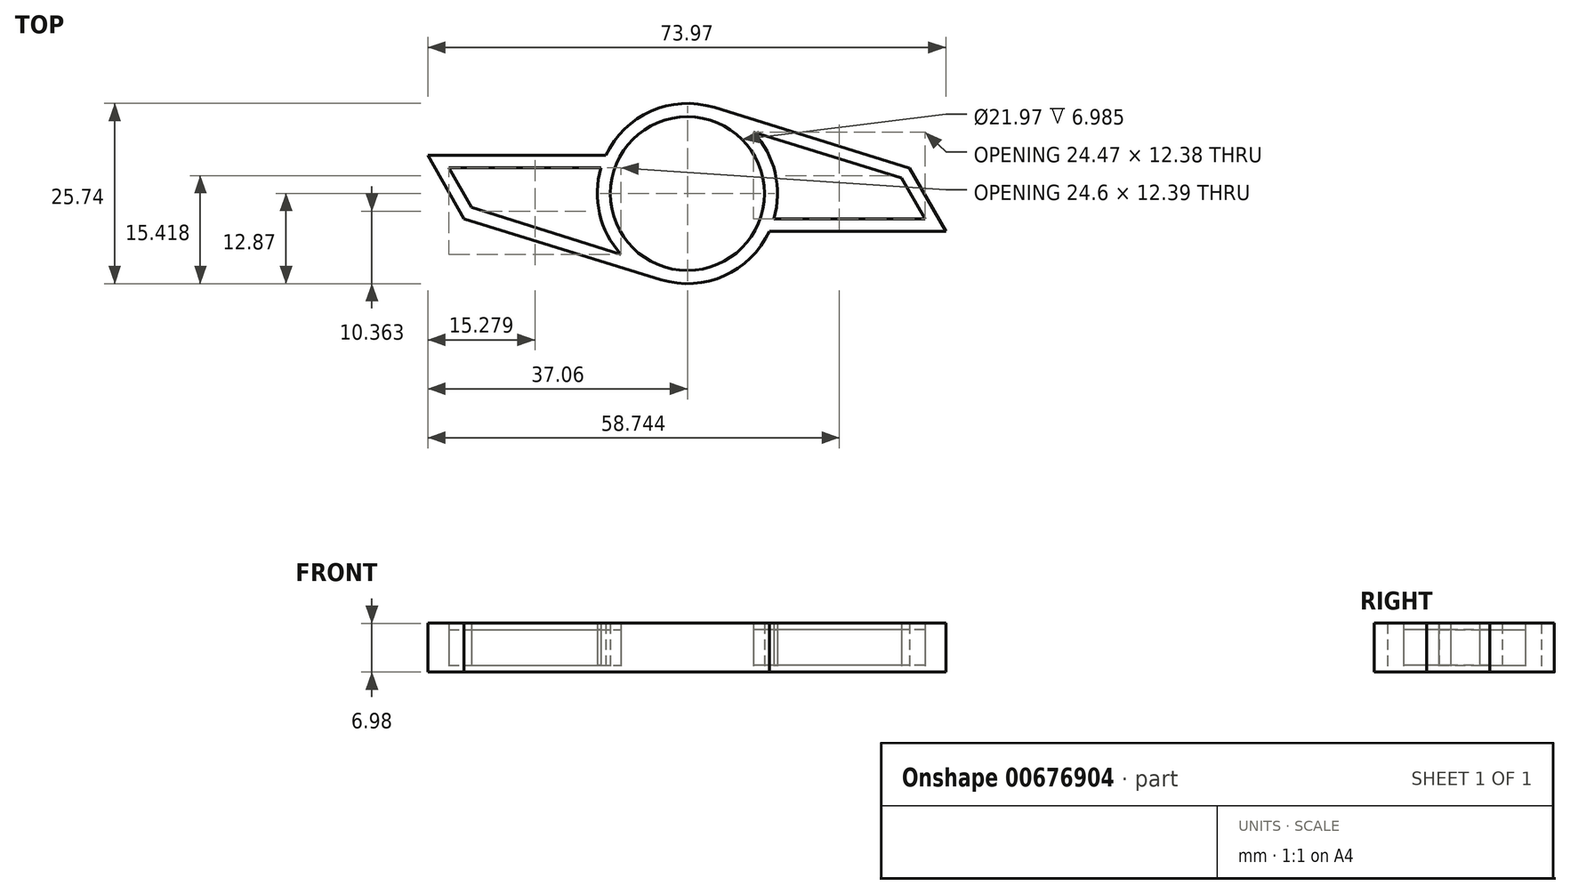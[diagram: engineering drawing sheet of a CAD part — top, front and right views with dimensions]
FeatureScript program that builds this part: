
annotation { "Feature Type Name" : "Feature", "Feature Type Description" : "" }
export const myFeature = defineFeature(function(context is Context, id is Id, definition is map)
    precondition{}
    {
        {
            var Q0;
            Q0=qCreatedBy(makeId("Top.planeOp"),FACE);
            var sketch = newSketch(context, id + "F0", { "sketchPlane" : qUnion([Q0])});
            skCircle(sketch, "E0", {"center": v(0, 0) * mm, "radius": 10.99 * mm});
            skCircle(sketch, "E1", {"center": v(0, 0) * mm, "radius": 12.87 * mm});
            skLineSegment(sketch, "E2", {"start": v(11.7, -5.37) * mm, "end": v(36.91, -5.37) * mm});
            skLineSegment(sketch, "E3", {"start": v(36.91, -5.37) * mm, "end": v(31.7, 3.65) * mm});
            skLineSegment(sketch, "E4", {"start": v(31.7, 3.65) * mm, "end": v(3.8, 12.3) * mm});
            skLineSegment(sketch, "E5", {"start": v(-11.66, 5.44) * mm, "end": v(-37.06, 5.44) * mm});
            skLineSegment(sketch, "E6", {"start": v(-37.06, 5.44) * mm, "end": v(-31.88, -3.6) * mm});
            skLineSegment(sketch, "E7", {"start": v(-31.88, -3.6) * mm, "end": v(-3.8, -12.3) * mm});
            skLineSegment(sketch, "E8", {"start": v(-34.08, 3.69) * mm, "end": v(-12.33, 3.69) * mm});
            skLineSegment(sketch, "E9", {"start": v(-34.08, 3.69) * mm, "end": v(-30.85, -1.94) * mm});
            skLineSegment(sketch, "E10", {"start": v(-30.85, -1.94) * mm, "end": v(-9.48, -8.7) * mm});
            skLineSegment(sketch, "E11", {"start": v(33.92, -3.64) * mm, "end": v(12.34, -3.64) * mm});
            skLineSegment(sketch, "E12", {"start": v(33.92, -3.64) * mm, "end": v(30.55, 2.2) * mm});
            skLineSegment(sketch, "E13", {"start": v(30.55, 2.2) * mm, "end": v(9.45, 8.74) * mm});
            skSolve(sketch);
        }
        {
            var Q0;
            {var subQ0=sQuery(id+"F0.wireOp",EDGE,"E8");Q0=makeQuery(id+"F0.imprint","IMPRINT",FACE,{"disambiguationData":[TD([[makeQuery(id+"F0.imprint","IMPRINT",EDGE,{"derivedFrom":subQ0}),-1.0]])]});}
            var Q1;
            {var subQ0=sQuery(id+"F0.wireOp",EDGE,"E11");Q1=makeQuery(id+"F0.imprint","IMPRINT",FACE,{"disambiguationData":[TD([[makeQuery(id+"F0.imprint","IMPRINT",EDGE,{"derivedFrom":subQ0}),-1.0]])]});}
            extrude(context, id + "F1", {"entities" : qUnion([Q0, Q1]), "endBound" : BoundingType.SYMMETRIC, "depth" : 5.08 * mm, "offsetDistance" : 25.4 * mm});
        }
        {
            var Q0;
            Q0 = qSketchRegion(id + "F0", true);
            extrude(context, id + "F2", {"entities" : qUnion([Q0]), "endBound" : BoundingType.SYMMETRIC, "depth" : 7 * mm, "offsetDistance" : 25.4 * mm});
        }
    });
